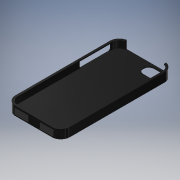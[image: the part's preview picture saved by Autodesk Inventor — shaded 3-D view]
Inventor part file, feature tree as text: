
AUTODESK INVENTOR PART (.ipt)
format: ipt  version: 2019 (Build 230136000, 136)  size: 377,344 bytes
history: native  units: mm
features: sketch x15, extrude x14, other x1, sweep x1, fillet x1
ambient origin geometry x8: Origin, YZ Plane, XZ Plane, XY Plane, X Axis, Y Axis, Z Axis, Center Point
bodies: Body1 (feature_tree)
feature tree (32):
  other  "솔리드1"
  extrude  "돌출1"  Depth=124.3mm
  sketch  "스케치2"
  sweep  "스윕1"
  extrude  "돌출2"  Depth=8.9mm
  extrude  "돌출3"  TaperAngle=0.0deg  [1 undecoded]
  extrude  "돌출6"  Depth=1.0mm
  extrude  "Extrusion8"  TaperAngle=0.0deg  [1 undecoded]
  fillet  "Fillet8"  Radius=44.0mm
  extrude  "Extrusion9"  Depth=22.0mm
  extrude  "Extrusion10"  Depth=6.0mm
  extrude  "Extrusion11"  Depth=2.0mm
  extrude  "Extrusion12"  Depth=1.0mm TaperAngle=0.0deg
  extrude  "Extrusion13"  TaperAngle=0.0deg  [1 undecoded]
  extrude  "Extrusion14"  Depth=1.0mm
  extrude  "Extrusion15"  TaperAngle=0.0deg  [1 undecoded]
  extrude  "Extrusion16"  Depth=9.9mm
  extrude  "Extrusion17"  TaperAngle=90.0deg  [1 undecoded]
  sketch  "스케치1"
  sketch  "스케치5"
  sketch  "스케치6"
  sketch  "스케치9"
  sketch  "Sketch12"  dims[d0=59.0mm d1=124.3mm]
  sketch  "Sketch13"  dims[d2=9.3mm d3=1.0mm d4=0.0mm]
  sketch  "Sketch14"  dims[d5=8.9mm d6=1.3mm]
  sketch  "Sketch15"  dims[d7=1.0mm d9=0.0mm]
  sketch  "Sketch16"  dims[d12=44.0mm d13=1.0mm]
  sketch  "Sketch17"  dims[d14=22.0mm d15=0.0mm d16=0.0mm d17=44.0mm]
  sketch  "Sketch18"  dims[d18=22.0mm d19=62.15mm]
  sketch  "Sketch19"  dims[d20=1.0mm d21=0.0mm d36=6.0mm]
  sketch  "Sketch20"  dims[d37=8.0mm d38=2.0mm]
  sketch  "Sketch21"  dims[d39=11.5mm d40=1.0mm d41=0.0mm d44=0.0mm d45=1.0mm d46=0.0mm d47=9.9mm d48=90.0deg d50=2.3mm d51=35.0mm d52=90.0deg d53=8.9mm d54=90.0deg d55=35.0mm d56=90.0deg d57=8.9mm d58=90.0deg d59=1.5mm d60=180.0deg d61=35.0mm d62=90.0deg d63=7.4mm d64=35.0mm d65=10.0mm d66=0.0mm d67=2.0mm d68=44.0mm d69=1.0mm d70=0.8415mm d71=0.0mm d72=44.0mm d73=1.0mm d74=0.8415mm d75=0.0mm d76=22.0mm d77=180.0deg d78=6.0mm d79=1.0mm d80=6.0mm d81=1.0mm d82=8.9mm d83=0.0mm d84=1.0mm d85=2.347mm d86=44.0mm d87=0.0mm d88=1.0mm d89=1.017mm d90=21.0mm d91=90.0deg d92=0.5mm d93=85.0mm d94=0.5mm d95=85.0mm d96=2.1mm d97=0.0mm d98=1.0mm d99=85.0mm d100=1.1mm d101=2.1mm d102=0.0mm d103=0.0mm d104=24.7mm d105=180.0deg d106=1.0mm d107=85.0mm d108=24.7mm d109=0.0mm d110=1.0mm d111=85.0mm d112=2.1mm d113=0.0mm d114=1.0mm d115=85.0mm d116=1.0mm d117=0.0mm d118=1.0mm d119=85.0mm d120=1.0mm d121=0.0mm]
note: 5 required parameter values undecoded (feature->parameter linkage not recoverable at this tier; creation-order binding heuristic only, values carry confidence <= 0.55)
